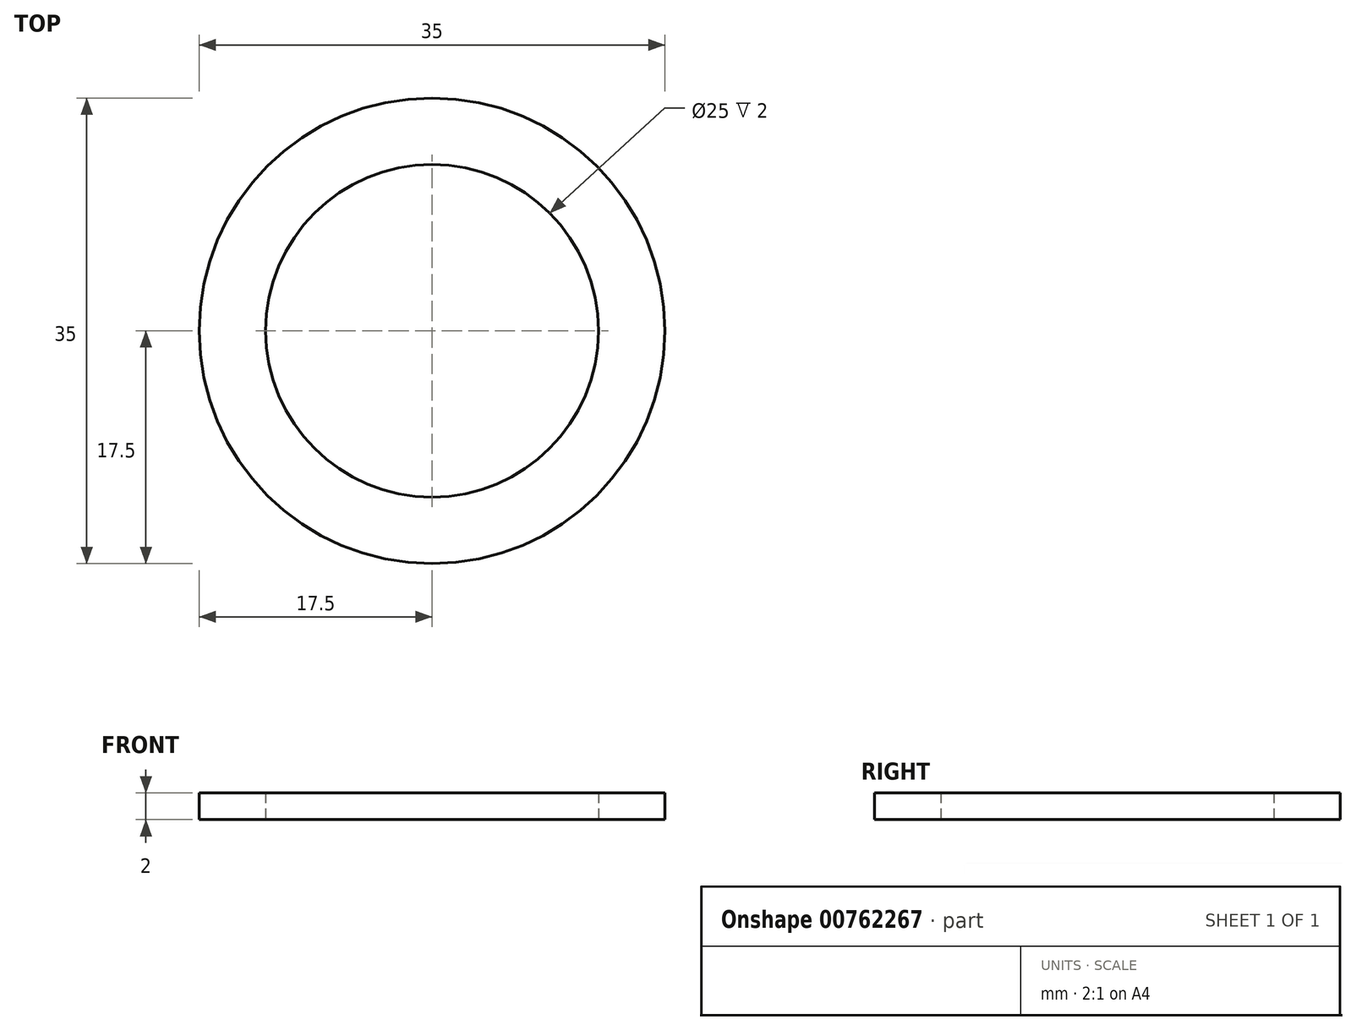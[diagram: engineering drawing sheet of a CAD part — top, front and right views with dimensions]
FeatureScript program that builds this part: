
annotation { "Feature Type Name" : "Feature", "Feature Type Description" : "" }
export const myFeature = defineFeature(function(context is Context, id is Id, definition is map)
    precondition{}
    {
        {
            var Q0;
            Q0=qCreatedBy(makeId("Top.planeOp"),FACE);
            var sketch = newSketch(context, id + "F0", { "sketchPlane" : qUnion([Q0])});
            skCircle(sketch, "E0", {"center": v(0, 0) * mm, "radius": 17.5 * mm});
            skCircle(sketch, "E1", {"center": v(0, 0) * mm, "radius": 12.5 * mm});
            skLineSegment(sketch, "E2", {"start": v(0, 17.5) * mm, "end": v(29.23, 17.5) * mm});
            skLineSegment(sketch, "E3", {"start": v(0, -17.5) * mm, "end": v(34.73, -17.5) * mm});
            skLineSegment(sketch, "E4.bottom", {"start": v(15, 17.5) * mm, "end": v(20, 17.5) * mm});
            skLineSegment(sketch, "E4.top", {"start": v(15, -17.5) * mm, "end": v(20, -17.5) * mm});
            skLineSegment(sketch, "E4.left", {"start": v(15, 17.5) * mm, "end": v(15, -17.5) * mm});
            skLineSegment(sketch, "E4.right", {"start": v(20, 17.5) * mm, "end": v(20, -17.5) * mm});
            skSolve(sketch);
        }
        {
            var Q0;
            Q0=makeQuery(id+"F0.imprint","IMPRINT",FACE,{"disambiguationData":[TD([[makeQuery(id+"F0.imprint","IMPRINT",EDGE,{"derivedFrom":sQuery(id+"F0.wireOp",EDGE,"E1")}),-1.0]])]});
            var Q1;
            {var subQ0=sQuery(id+"F0.wireOp",EDGE,"E4.left");var subQ1=sQuery(id+"F0.wireOp",EDGE,"E0");var subQ2=makeQuery(id+"F0.imprint","INTERSECT",VERTEX,{"disambiguationData":[OD(0.0)],"derivedFrom":[subQ1,subQ0]});Q1=makeQuery(id+"F0.imprint","IMPRINT",FACE,{"disambiguationData":[TD([[makeQuery(id+"F0.imprint","IMPRINT",EDGE,{"disambiguationData":[TD([[subQ2,1.0]])],"derivedFrom":subQ1}),1.0]])]});}
            var Q2;
            {var subQ1=sQuery(id+"F0.wireOp",EDGE,"E4.bottom");Q2=makeQuery(id+"F0.imprint","IMPRINT",FACE,{"disambiguationData":[TD([[makeQuery(id+"F0.imprint","IMPRINT",EDGE,{"derivedFrom":subQ1}),-1.0]])]});}
            extrude(context, id + "F1", {"entities" : qUnion([Q0, Q1, Q2]), "depth" : 2 * mm, "offsetDistance" : 25 * mm});
        }
        {
            var Q0;
            Q0=makeQuery(id+"F1.opExtrude","CAP_FACE",FACE,{"disambiguationData":[OSD([sQuery(id+"F0.wireOp",EDGE,"E0"),sQuery(id+"F0.wireOp",EDGE,"E1"),sQuery(id+"F0.wireOp",EDGE,"E4.bottom"),sQuery(id+"F0.wireOp",EDGE,"E4.top"),sQuery(id+"F0.wireOp",EDGE,"E4.left"),sQuery(id+"F0.wireOp",EDGE,"E4.right")])],"isStart":false});
            var sketch = newSketch(context, id + "F2", { "sketchPlane" : qUnion([Q0])});
            skCircle(sketch, "E5", {"center": v(17.5, 15) * mm, "radius": 1.5 * mm});
            skSolve(sketch);
        }
        {
            var Q0;
            Q0=makeQuery(id+"F2.imprint","IMPRINT",FACE,{"disambiguationData":[TD([[makeQuery(id+"F2.imprint","IMPRINT",EDGE,{"derivedFrom":sQuery(id+"F2.wireOp",EDGE,"E5")}),1.0]])]});
            extrude(context, id + "F3", {"entities" : qUnion([Q0]), "operationType" : NewBodyOperationType.REMOVE, "oppositeDirection" : true, "depth" : 2 * mm, "offsetDistance" : 25 * mm});
        }
        {
            var Q0;
            Q0=makeQuery(id+"F1.opExtrude","CAP_FACE",FACE,{"disambiguationData":[OSD([sQuery(id+"F0.wireOp",EDGE,"E0"),sQuery(id+"F0.wireOp",EDGE,"E1"),sQuery(id+"F0.wireOp",EDGE,"E4.bottom"),sQuery(id+"F0.wireOp",EDGE,"E4.top"),sQuery(id+"F0.wireOp",EDGE,"E4.left"),sQuery(id+"F0.wireOp",EDGE,"E4.right")])],"isStart":false});
            var sketch = newSketch(context, id + "F4", { "sketchPlane" : qUnion([Q0])});
            skText(sketch, "E6", { "text": "eTEK", "fontName": "OpenSans-Bold.ttf"});
            const initialGuessF4  = {"E6": [0.0194, -0.00901, 0, 1, 0.0044]};
            skSetInitialGuess(sketch, initialGuessF4);
            skSolve(sketch);
        }
        {
            var Q0;
            Q0=makeQuery(id+"F4.imprint","IMPRINT",FACE,{"disambiguationData":[TD([[makeQuery(id+"F4.imprint","IMPRINT",EDGE,{"derivedFrom":sQuery(id+"F4.wireOp",EDGE,"E6.sketch_text.stroke-0")}),-1.0]])]});
            var Q1;
            Q1=makeQuery(id+"F4.imprint","IMPRINT",FACE,{"disambiguationData":[TD([[makeQuery(id+"F4.imprint","IMPRINT",EDGE,{"derivedFrom":sQuery(id+"F4.wireOp",EDGE,"E6.sketch_text.stroke-20")}),-1.0]])]});
            var Q2;
            Q2=makeQuery(id+"F4.imprint","IMPRINT",FACE,{"disambiguationData":[TD([[makeQuery(id+"F4.imprint","IMPRINT",EDGE,{"derivedFrom":sQuery(id+"F4.wireOp",EDGE,"E6.sketch_text.stroke-28")}),-1.0]])]});
            var Q3;
            Q3=makeQuery(id+"F4.imprint","IMPRINT",FACE,{"disambiguationData":[TD([[makeQuery(id+"F4.imprint","IMPRINT",EDGE,{"derivedFrom":sQuery(id+"F4.wireOp",EDGE,"E6.sketch_text.stroke-40")}),-1.0]])]});
            extrude(context, id + "F5", {"entities" : qUnion([Q0, Q1, Q2, Q3]), "operationType" : NewBodyOperationType.REMOVE, "oppositeDirection" : true, "depth" : 1 * mm, "offsetDistance" : 25 * mm});
        }
    });
